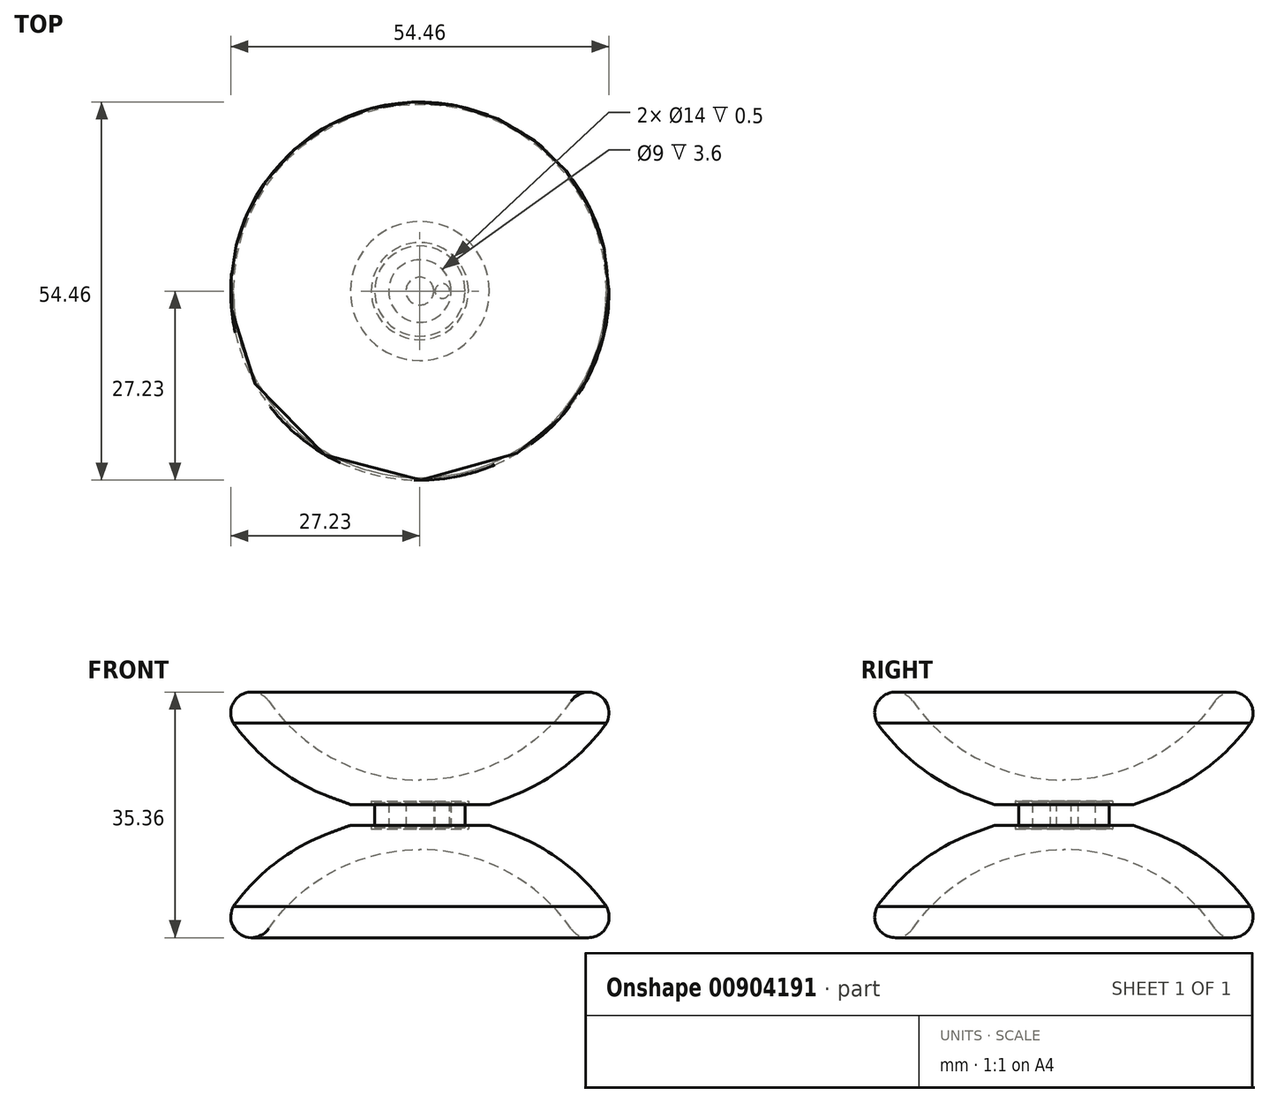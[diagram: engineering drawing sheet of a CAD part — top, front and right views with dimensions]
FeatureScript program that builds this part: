
annotation { "Feature Type Name" : "Feature", "Feature Type Description" : "" }
export const myFeature = defineFeature(function(context is Context, id is Id, definition is map)
    precondition{}
    {
        {
            var Q0;
            Q0=qCreatedBy(makeId("Front.planeOp"),FACE);
            var sketch = newSketch(context, id + "F0", { "sketchPlane" : qUnion([Q0])});
            skLineSegment(sketch, "E0", {"start": v(-42, 0) * mm, "end": v(42, 0) * mm, "construction": true});
            skLineSegment(sketch, "E1", {"start": v(0, 0) * mm, "end": v(0, 30.8) * mm, "construction": true});
            skLineSegment(sketch, "E2", {"start": v(2, 22) * mm, "end": v(2, 18) * mm});
            skLineSegment(sketch, "E3", {"start": v(2, 18) * mm, "end": v(7, 18) * mm});
            skLineSegment(sketch, "E4", {"start": v(2, 22) * mm, "end": v(7, 22) * mm});
            skLineSegment(sketch, "E5", {"start": v(23.83, 26.6) * mm, "end": v(30, 40) * mm});
            skLineSegment(sketch, "E6", {"start": v(23.83, 13.4) * mm, "end": v(30, 0) * mm});
            skLineSegment(sketch, "E7.trimOffspring", {"start": v(23.83, 13.4) * mm, "end": v(10, 18.5) * mm});
            skLineSegment(sketch, "E8.trimOffspring", {"start": v(23.83, 26.6) * mm, "end": v(10, 21.5) * mm});
            skPoint(sketch, "E9", {"position": v(2, 20) * mm});
            skPoint(sketch, "E10", {"position": v(0, 20) * mm});
            skLineSegment(sketch, "E11", {"start": v(0, 20) * mm, "end": v(35.14, 20) * mm, "construction": true});
            skLineSegment(sketch, "E12", {"start": v(7, 21.5) * mm, "end": v(7, 22) * mm});
            skLineSegment(sketch, "E13", {"start": v(7, 18.5) * mm, "end": v(7, 18) * mm});
            skLineSegment(sketch, "E14.bottom", {"start": v(4.5, 21.8) * mm, "end": v(6.5, 21.8) * mm});
            skLineSegment(sketch, "E14.top", {"start": v(4.5, 18.2) * mm, "end": v(6.5, 18.2) * mm});
            skLineSegment(sketch, "E14.left", {"start": v(4.5, 21.8) * mm, "end": v(4.5, 18.2) * mm});
            skLineSegment(sketch, "E14.right", {"start": v(6.5, 21.8) * mm, "end": v(6.5, 18.2) * mm});
            skPoint(sketch, "E15", {"position": v(4.5, 20) * mm});
            skLineSegment(sketch, "E16", {"start": v(30, 0) * mm, "end": v(24, 0) * mm});
            skLineSegment(sketch, "E17", {"start": v(24, 0) * mm, "end": v(15, 15) * mm});
            skLineSegment(sketch, "E18", {"start": v(15, 15) * mm, "end": v(0, 15) * mm});
            skLineSegment(sketch, "E19", {"start": v(0, 15) * mm, "end": v(0, 25) * mm});
            skLineSegment(sketch, "E20", {"start": v(0, 25) * mm, "end": v(15, 25) * mm});
            skLineSegment(sketch, "E21", {"start": v(15, 25) * mm, "end": v(24, 40) * mm});
            skLineSegment(sketch, "E22", {"start": v(24, 40) * mm, "end": v(30, 40) * mm});
            skLineSegment(sketch, "E23", {"start": v(7, 21.5) * mm, "end": v(10, 21.5) * mm});
            skLineSegment(sketch, "E24", {"start": v(7, 18.5) * mm, "end": v(10, 18.5) * mm});
            skLineSegment(sketch, "E25.bottom", {"start": v(2.2, 21.8) * mm, "end": v(4.3, 21.8) * mm});
            skLineSegment(sketch, "E25.top", {"start": v(2.2, 18.2) * mm, "end": v(4.3, 18.2) * mm});
            skLineSegment(sketch, "E25.left", {"start": v(2.2, 21.8) * mm, "end": v(2.2, 18.2) * mm});
            skLineSegment(sketch, "E25.right", {"start": v(4.3, 21.8) * mm, "end": v(4.3, 18.2) * mm});
            skLineSegment(sketch, "E26", {"start": v(3.25, 21.8) * mm, "end": v(3.25, 18.2) * mm});
            skSolve(sketch);
        }
        {
            var Q0;
            {var subQ0=sQuery(id+"F0.wireOp",EDGE,"E25.right");Q0=makeQuery(id+"F0.imprint","IMPRINT",FACE,{"disambiguationData":[TD([[makeQuery(id+"F0.imprint","IMPRINT",EDGE,{"derivedFrom":subQ0}),-1.0]])]});}
            var Q1;
            Q1=sQuery(id+"F0.wireOp",EDGE,"E26");
            revolve(context, id + "F1", {"surfaceOperationType" : NewSurfaceOperationType.NEW, "entities" : qUnion([Q0]), "axis" : qUnion([Q1]), "revolveType" : RevolveType.FULL});
        }
        {
            var Q0;
            Q0=makeQuery(id+"F0.imprint","IMPRINT",FACE,{"disambiguationData":[TD([[makeQuery(id+"F0.imprint","IMPRINT",EDGE,{"derivedFrom":sQuery(id+"F0.wireOp",EDGE,"E14.bottom")}),-1.0]])]});
            var Q1;
            Q1=makeQuery(id+"F0.imprint","IMPRINT",FACE,{"disambiguationData":[TD([[makeQuery(id+"F0.imprint","IMPRINT",EDGE,{"derivedFrom":sQuery(id+"F0.wireOp",EDGE,"E2")}),-1.0]])]});
            var Q2;
            Q2=sQuery(id+"F0.wireOp",EDGE,"E1");
            revolve(context, id + "F2", {"surfaceOperationType" : NewSurfaceOperationType.NEW, "entities" : qUnion([Q0, Q1]), "axis" : qUnion([Q2]), "revolveType" : RevolveType.FULL});
        }
        {
            var Q0;
            Q0=makeQuery(id+"F2.opRevolve","SWEPT_EDGE",EDGE,{"disambiguationData":[OSD([sQuery(id+"F0.wireOp",EDGE,"E20"),sQuery(id+"F0.wireOp",EDGE,"E21")])]});
            var Q1;
            Q1=makeQuery(id+"F2.opRevolve","SWEPT_EDGE",EDGE,{"disambiguationData":[OSD([sQuery(id+"F0.wireOp",EDGE,"E17"),sQuery(id+"F0.wireOp",EDGE,"E18")])]});
            fillet(context, id + "F3", {"entities" : qUnion([Q0, Q1]), "radius" : 26.5 * mm, "tangentPropagation" : true, "allowEdgeOverflow" : false});
        }
        {
            var Q0;
            Q0=makeQuery(id+"F2.opRevolve","SWEPT_EDGE",EDGE,{"disambiguationData":[OSD([sQuery(id+"F0.wireOp",EDGE,"E6"),sQuery(id+"F0.wireOp",EDGE,"E16")])]});
            var Q1;
            Q1=makeQuery(id+"F2.opRevolve","SWEPT_EDGE",EDGE,{"disambiguationData":[OSD([sQuery(id+"F0.wireOp",EDGE,"E5"),sQuery(id+"F0.wireOp",EDGE,"E22")])]});
            fillet(context, id + "F4", {"entities" : qUnion([Q0, Q1]), "radius" : 5 * mm, "tangentPropagation" : true, "allowEdgeOverflow" : false});
        }
        {
            var Q0;
            Q0=makeQuery(id+"F4.opFillet","BLEND_EDGE",EDGE,{"blendedFrom":[makeQuery(id+"F2.opRevolve","SWEPT_EDGE",EDGE,{"disambiguationData":[OSD([sQuery(id+"F0.wireOp",EDGE,"E5"),sQuery(id+"F0.wireOp",EDGE,"E22")])]}),makeQuery(id+"F2.opRevolve","SWEPT_FACE",FACE,{"disambiguationData":[OSD([sQuery(id+"F0.wireOp",EDGE,"E21")])]})],"blendedInto":[makeQuery(id+"F2.opRevolve","SWEPT_FACE",FACE,{"disambiguationData":[OSD([sQuery(id+"F0.wireOp",EDGE,"E21")])]})]});
            var Q1;
            Q1=makeQuery(id+"F4.opFillet","BLEND_EDGE",EDGE,{"blendedFrom":[makeQuery(id+"F2.opRevolve","SWEPT_EDGE",EDGE,{"disambiguationData":[OSD([sQuery(id+"F0.wireOp",EDGE,"E6"),sQuery(id+"F0.wireOp",EDGE,"E16")])]}),makeQuery(id+"F2.opRevolve","SWEPT_FACE",FACE,{"disambiguationData":[OSD([sQuery(id+"F0.wireOp",EDGE,"E17")])]})],"blendedInto":[makeQuery(id+"F2.opRevolve","SWEPT_FACE",FACE,{"disambiguationData":[OSD([sQuery(id+"F0.wireOp",EDGE,"E17")])]})]});
            fillet(context, id + "F5", {"entities" : qUnion([Q0, Q1]), "radius" : 3 * mm, "tangentPropagation" : true, "allowEdgeOverflow" : false});
        }
        {
            var Q0;
            Q0=makeQuery(id+"F2.opRevolve","SWEPT_EDGE",EDGE,{"disambiguationData":[OSD([sQuery(id+"F0.wireOp",EDGE,"E5"),sQuery(id+"F0.wireOp",EDGE,"E8.trimOffspring")])]});
            var Q1;
            Q1=makeQuery(id+"F2.opRevolve","SWEPT_EDGE",EDGE,{"disambiguationData":[OSD([sQuery(id+"F0.wireOp",EDGE,"E6"),sQuery(id+"F0.wireOp",EDGE,"E7.trimOffspring")])]});
            fillet(context, id + "F6", {"entities" : qUnion([Q0, Q1]), "radius" : 30 * mm, "tangentPropagation" : true, "allowEdgeOverflow" : false});
        }
    });
